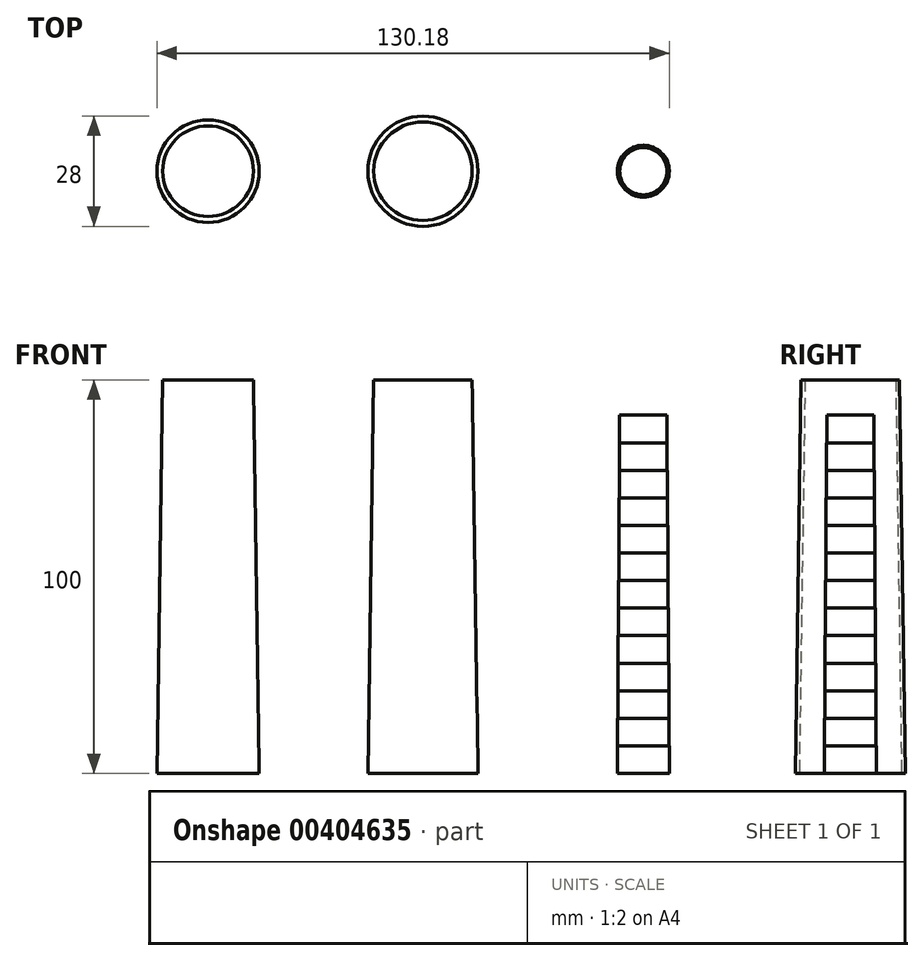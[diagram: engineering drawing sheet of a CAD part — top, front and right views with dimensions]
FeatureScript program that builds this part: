
annotation { "Feature Type Name" : "Feature", "Feature Type Description" : "" }
export const myFeature = defineFeature(function(context is Context, id is Id, definition is map)
    precondition{}
    {
        {
            var Q0;
            Q0=qCreatedBy(makeId("Top.planeOp"),FACE);
            var sketch = newSketch(context, id + "F0", { "sketchPlane" : qUnion([Q0])});
            skCircle(sketch, "E0", {"center": v(0, 0) * mm, "radius": 6.6 * mm});
            skSolve(sketch);
        }
        {
            var Q0;
            Q0 = qSketchRegion(id + "F0", true);
            extrude(context, id + "F1", {"entities" : qUnion([Q0]), "depth" : 7 * mm, "offsetDistance" : 25 * mm});
        }
        {
            var Q0;
            Q0=makeQuery(id+"F1.opExtrude","CAP_FACE",FACE,{"disambiguationData":[OSD([sQuery(id+"F0.wireOp",EDGE,"E0")])],"isStart":false});
            var sketch = newSketch(context, id + "F2", { "sketchPlane" : qUnion([Q0])});
            skCircle(sketch, "E1.0", {"center": v(0, 0) * mm, "radius": 6.55 * mm});
            skSolve(sketch);
        }
        {
            var Q0;
            Q0 = qSketchRegion(id + "F2", true);
            extrude(context, id + "F3", {"entities" : qUnion([Q0]), "operationType" : NewBodyOperationType.ADD, "depth" : 7 * mm, "offsetDistance" : 25 * mm});
        }
        {
            var Q0;
            Q0=makeQuery(id+"F3.opExtrude","CAP_FACE",FACE,{"disambiguationData":[OSD([sQuery(id+"F2.wireOp",EDGE,"E1.0")])],"isStart":false});
            var sketch = newSketch(context, id + "F4", { "sketchPlane" : qUnion([Q0])});
            skCircle(sketch, "E2", {"center": v(0, 0) * mm, "radius": 6.5 * mm});
            skSolve(sketch);
        }
        {
            var Q0;
            Q0 = qSketchRegion(id + "F4", true);
            extrude(context, id + "F5", {"entities" : qUnion([Q0]), "operationType" : NewBodyOperationType.ADD, "depth" : 7 * mm, "offsetDistance" : 25 * mm});
        }
        {
            var Q0;
            Q0=makeQuery(id+"F5.opExtrude","CAP_FACE",FACE,{"disambiguationData":[OSD([sQuery(id+"F4.wireOp",EDGE,"E2")])],"isStart":false});
            var sketch = newSketch(context, id + "F6", { "sketchPlane" : qUnion([Q0])});
            skCircle(sketch, "E3", {"center": v(0, 0) * mm, "radius": 6.45 * mm});
            skSolve(sketch);
        }
        {
            var Q0;
            Q0 = qSketchRegion(id + "F6", true);
            extrude(context, id + "F7", {"entities" : qUnion([Q0]), "operationType" : NewBodyOperationType.ADD, "depth" : 7 * mm, "offsetDistance" : 25 * mm});
        }
        {
            var Q0;
            Q0=makeQuery(id+"F7.opExtrude","CAP_FACE",FACE,{"disambiguationData":[OSD([sQuery(id+"F6.wireOp",EDGE,"E3")])],"isStart":false});
            var sketch = newSketch(context, id + "F8", { "sketchPlane" : qUnion([Q0])});
            skCircle(sketch, "E4", {"center": v(0, 0) * mm, "radius": 6.4 * mm});
            skSolve(sketch);
        }
        {
            var Q0;
            Q0 = qSketchRegion(id + "F8", true);
            extrude(context, id + "F9", {"entities" : qUnion([Q0]), "operationType" : NewBodyOperationType.ADD, "depth" : 7 * mm, "offsetDistance" : 25 * mm});
        }
        {
            var Q0;
            Q0=makeQuery(id+"F9.opExtrude","CAP_FACE",FACE,{"disambiguationData":[OSD([sQuery(id+"F8.wireOp",EDGE,"E4")])],"isStart":false});
            var sketch = newSketch(context, id + "F10", { "sketchPlane" : qUnion([Q0])});
            skCircle(sketch, "E5.0", {"center": v(0, 0) * mm, "radius": 6.35 * mm});
            skSolve(sketch);
        }
        {
            var Q0;
            Q0 = qSketchRegion(id + "F10", true);
            extrude(context, id + "F11", {"entities" : qUnion([Q0]), "operationType" : NewBodyOperationType.ADD, "depth" : 7 * mm, "offsetDistance" : 25 * mm});
        }
        {
            var Q0;
            Q0=makeQuery(id+"F11.opExtrude","CAP_FACE",FACE,{"disambiguationData":[OSD([sQuery(id+"F10.wireOp",EDGE,"E5.0")])],"isStart":false});
            var sketch = newSketch(context, id + "F12", { "sketchPlane" : qUnion([Q0])});
            skCircle(sketch, "E6.0", {"center": v(0, 0) * mm, "radius": 6.3 * mm});
            skSolve(sketch);
        }
        {
            var Q0;
            Q0 = qSketchRegion(id + "F12", true);
            extrude(context, id + "F13", {"entities" : qUnion([Q0]), "operationType" : NewBodyOperationType.ADD, "depth" : 7 * mm, "offsetDistance" : 25 * mm});
        }
        {
            var Q0;
            Q0=makeQuery(id+"F13.opExtrude","CAP_FACE",FACE,{"disambiguationData":[OSD([sQuery(id+"F12.wireOp",EDGE,"E6.0")])],"isStart":false});
            var sketch = newSketch(context, id + "F14", { "sketchPlane" : qUnion([Q0])});
            skCircle(sketch, "E7.0", {"center": v(0, 0) * mm, "radius": 6.25 * mm});
            skSolve(sketch);
        }
        {
            var Q0;
            Q0 = qSketchRegion(id + "F14", true);
            extrude(context, id + "F15", {"entities" : qUnion([Q0]), "operationType" : NewBodyOperationType.ADD, "depth" : 7 * mm, "offsetDistance" : 25 * mm});
        }
        {
            var Q0;
            Q0=makeQuery(id+"F15.opExtrude","CAP_FACE",FACE,{"disambiguationData":[OSD([sQuery(id+"F14.wireOp",EDGE,"E7.0")])],"isStart":false});
            var sketch = newSketch(context, id + "F16", { "sketchPlane" : qUnion([Q0])});
            skCircle(sketch, "E8.0", {"center": v(0, 0) * mm, "radius": 6.2 * mm});
            skSolve(sketch);
        }
        {
            var Q0;
            Q0 = qSketchRegion(id + "F16", true);
            extrude(context, id + "F17", {"entities" : qUnion([Q0]), "operationType" : NewBodyOperationType.ADD, "depth" : 7 * mm, "offsetDistance" : 25 * mm});
        }
        {
            var Q0;
            Q0=makeQuery(id+"F17.opExtrude","CAP_FACE",FACE,{"disambiguationData":[OSD([sQuery(id+"F16.wireOp",EDGE,"E8.0")])],"isStart":false});
            var sketch = newSketch(context, id + "F18", { "sketchPlane" : qUnion([Q0])});
            skCircle(sketch, "E9.0", {"center": v(0, 0) * mm, "radius": 6.15 * mm});
            skSolve(sketch);
        }
        {
            var Q0;
            Q0 = qSketchRegion(id + "F18", true);
            extrude(context, id + "F19", {"entities" : qUnion([Q0]), "operationType" : NewBodyOperationType.ADD, "depth" : 7 * mm, "offsetDistance" : 25 * mm});
        }
        {
            var Q0;
            Q0=makeQuery(id+"F19.opExtrude","CAP_FACE",FACE,{"disambiguationData":[OSD([sQuery(id+"F18.wireOp",EDGE,"E9.0")])],"isStart":false});
            var sketch = newSketch(context, id + "F20", { "sketchPlane" : qUnion([Q0])});
            skCircle(sketch, "E10.0", {"center": v(0, 0) * mm, "radius": 6.1 * mm});
            skSolve(sketch);
        }
        {
            var Q0;
            Q0 = qSketchRegion(id + "F20", true);
            extrude(context, id + "F21", {"entities" : qUnion([Q0]), "operationType" : NewBodyOperationType.ADD, "depth" : 7 * mm, "offsetDistance" : 25 * mm});
        }
        {
            var Q0;
            Q0=makeQuery(id+"F21.opExtrude","CAP_FACE",FACE,{"disambiguationData":[OSD([sQuery(id+"F20.wireOp",EDGE,"E10.0")])],"isStart":false});
            var sketch = newSketch(context, id + "F22", { "sketchPlane" : qUnion([Q0])});
            skCircle(sketch, "E11.0", {"center": v(0, 0) * mm, "radius": 6.05 * mm});
            skSolve(sketch);
        }
        {
            var Q0;
            Q0 = qSketchRegion(id + "F22", true);
            extrude(context, id + "F23", {"entities" : qUnion([Q0]), "operationType" : NewBodyOperationType.ADD, "depth" : 7 * mm, "offsetDistance" : 25 * mm});
        }
        {
            var Q0;
            Q0=makeQuery(id+"F23.opExtrude","CAP_FACE",FACE,{"disambiguationData":[OSD([sQuery(id+"F22.wireOp",EDGE,"E11.0")])],"isStart":false});
            var sketch = newSketch(context, id + "F24", { "sketchPlane" : qUnion([Q0])});
            skCircle(sketch, "E12.0", {"center": v(0, 0) * mm, "radius": 6 * mm});
            skSolve(sketch);
        }
        {
            var Q0;
            Q0 = qSketchRegion(id + "F24", true);
            extrude(context, id + "F25", {"entities" : qUnion([Q0]), "operationType" : NewBodyOperationType.ADD, "depth" : 7 * mm, "offsetDistance" : 25 * mm});
        }
        {
            var Q0;
            Q0=qCreatedBy(makeId("Top.planeOp"), FACE);
            var sketch = newSketch(context, id + "F26", { "sketchPlane" : qUnion([Q0])});
            skCircle(sketch, "E13", {"center": v(-56, 0) * mm, "radius": 14 * mm});
            skCircle(sketch, "E14", {"center": v(-110.58, 0) * mm, "radius": 13 * mm});
            skSolve(sketch);
        }
        {
            var Q0;
            Q0 = qSketchRegion(id + "F26", true);
            extrude(context, id + "F27", {"entities" : qUnion([Q0]), "domain" : OperationDomain.MODEL, "flatOperationType" : FlatOperationType.REMOVE, "depth" : 100 * mm, "offsetDistance" : 25 * mm, "hasDraft" : true, "draftAngle" : 0.85 * degree, "draftPullDirection" : true});
        }
    });
